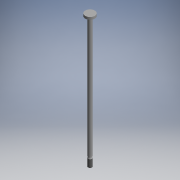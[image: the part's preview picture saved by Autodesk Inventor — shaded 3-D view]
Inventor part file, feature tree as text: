
AUTODESK INVENTOR PART (.ipt)
format: ipt  version: 2017.3 (Build 213256000, 256)  size: 133,120 bytes
history: native  units: mm (DEFAULTED — no unit token found)
features: other x28, sketch x3, revolve x2, thread x1, extrude x1
ambient origin geometry x8: Origin, YZ Plane, XZ Plane, XY Plane, X Axis, Y Axis, Z Axis, Center Point
bodies: Solid1 (feature_tree)
feature tree (35):
  revolve  "Revolution1"  Angle=360.0deg
  revolve  "Revolution2"  [1 undecoded]
  thread  "Thread1"  [1 undecoded]
  extrude  "Extrusion1"  [1 undecoded]
  other  "FDT_KSAUFSATZ_XY"
  other  "FDT_KSAUFSATZ_YZ"
  other  "FDT_KSAUFSATZ_ZX"
  other  "FDT_KSAUFSATZ_X"
  other  "FDT_KSAUFSATZ_Y"
  other  "FDT_KSAUFSATZ_Z"
  other  "FDT_KSAUFSATZ_Center"
  other  "FDT_NUT_XY"
  other  "FDT_NUT_YZ"
  other  "FDT_NUT_ZX"
  other  "FDT_NUT_X"
  other  "FDT_NUT_Y"
  other  "FDT_NUT_Z"
  other  "FDT_NUT_Center"
  other  "KS_XY"
  other  "KS_YZ"
  other  "KS_ZX"
  other  "KS_X"
  other  "KS_Y"
  other  "KS_Z"
  other  "KS_Center"
  other  "NUT1_XY"
  other  "NUT1_YZ"
  other  "NUT1_ZX"
  other  "NUT1_X"
  other  "NUT1_Y"
  other  "NUT1_Z"
  other  "NUT1_Center"
  sketch  "Sketch_2"  dims[d0=360.0deg d1=360.0deg]
  sketch  "Sketch_6"  dims[d2=15.535mm d3=0.0mm d4=4.0mm d5=0.0mm]
  sketch  "Sketch_7"
note: 3 required parameter values undecoded (feature->parameter linkage not recoverable at this tier; creation-order binding heuristic only, values carry confidence <= 0.55)